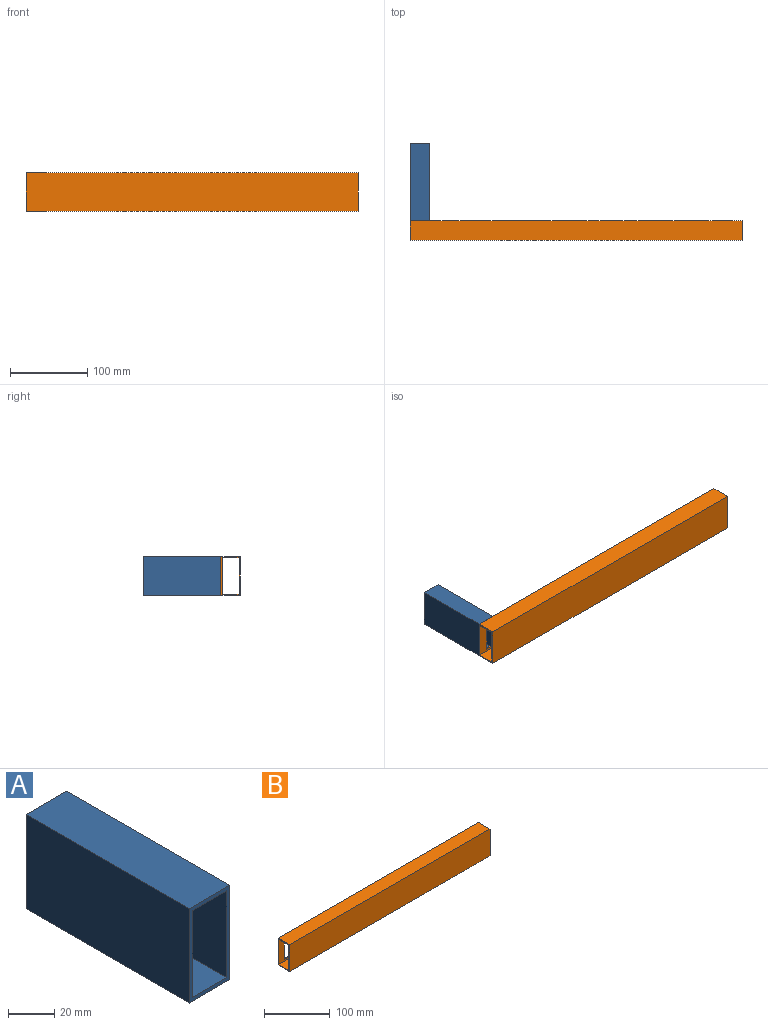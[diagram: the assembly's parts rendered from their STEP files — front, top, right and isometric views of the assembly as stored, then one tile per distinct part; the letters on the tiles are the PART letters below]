
ASSEMBLY  parts=2 mates=1
PART A: 10 faces, bbox 25x100x50 mm
  f0: plane 100x25mm, normal (0,0,1), area 2500mm2, adj f1,f7,f8,f9
  f1: plane 100x50mm, normal (-1,0,0), area 5000mm2, adj f0,f2,f8,f9
  f2: plane 100x25mm, normal (0,0,-1), area 2500mm2, adj f1,f7,f8,f9
  f3: plane 100x21mm, normal (0,0,-1), area 2100mm2, adj f4,f6,f8,f9
  f4: plane 100x46mm, normal (-1,0,0), area 4600mm2, adj f3,f5,f8,f9
  f5: plane 100x21mm, normal (0,0,1), area 2100mm2, adj f4,f6,f8,f9
  f6: plane 100x46mm, normal (1,0,0), area 4600mm2, adj f3,f5,f8,f9
  f7: plane 100x50mm, normal (1,0,0), area 5000mm2, adj f0,f2,f8,f9
  f8: plane 50x25mm, normal (0,-1,0), area 284mm2, adj f0,f1,f2,f3,f4,f5,f6,f7
  f9: plane 50x25mm, normal (0,1,0), area 284mm2, adj f0,f1,f2,f3,f4,f5,f6,f7
PART B: 72 faces, bbox 430x25x50 mm
  f0: plane 430x47mm, normal (0,1,0), area 20210mm2, adj f1,f7,f8,f9
  f1: plane 430x22mm, normal (0,0,-1), area 9460mm2, adj f0,f2,f8,f9
  f2: plane 430x47mm, normal (0,-1,0), area 11386.5mm2, adj f1,f7,f8,f9,f10,f11,f12,f13
  f3: plane 430x50mm, normal (0,1,0), area 12676.5mm2, adj f4,f6,f8,f9,f10,f11,f12,f13
  f4: plane 430x25mm, normal (0,0,1), area 10750mm2, adj f3,f5,f8,f9
  f5: plane 430x50mm, normal (0,-1,0), area 21500mm2, adj f4,f6,f8,f9
  f6: plane 430x25mm, normal (0,0,-1), area 10750mm2, adj f3,f5,f8,f9
  f7: plane 430x22mm, normal (0,0,1), area 9460mm2, adj f0,f2,f8,f9
  f8: plane 50x25mm, normal (1,0,0), area 216mm2, adj f0,f1,f2,f3,f4,f5,f6,f7
  f9: plane 50x25mm, normal (-1,0,0), area 216mm2, adj f0,f1,f2,f3,f4,f5,f6,f7
  f10: plane 40x21.56mm, normal (-0.88,0,-0.47), area 68.2mm2, adj f2,f3,f11,f12
  f11: plane 40x1.5mm, normal (1,0,0), area 60mm2, adj f2,f3,f10,f12
  f12: plane 21.56x1.5mm, normal (0,0,1), area 32.3mm2, adj f2,f3,f10,f11
  f13: plane 40x21.56mm, normal (-0.88,0,-0.47), area 68.2mm2, adj f2,f3,f14,f15
  f14: plane 40x1.5mm, normal (1,0,0), area 60mm2, adj f2,f3,f13,f15
  f15: plane 21.56x1.5mm, normal (0,0,1), area 32.3mm2, adj f2,f3,f13,f14
  f16: plane 40x21.56mm, normal (-0.88,0,-0.47), area 68.2mm2, adj f2,f3,f17,f18
  f17: plane 40x1.5mm, normal (1,0,0), area 60mm2, adj f2,f3,f16,f18
  f18: plane 21.56x1.5mm, normal (0,0,1), area 32.3mm2, adj f2,f3,f16,f17
  f19: plane 40x1.5mm, normal (-1,0,0), area 60mm2, adj f2,f3,f20,f21
  f20: plane 21.56x1.5mm, normal (0,0,-1), area 32.3mm2, adj f2,f3,f19,f21
  f21: plane 40x21.56mm, normal (0.88,0,0.47), area 68.2mm2, adj f2,f3,f19,f20
  f22: plane 40x21.56mm, normal (-0.88,0,-0.47), area 68.2mm2, adj f2,f3,f23,f24
  f23: plane 40x1.5mm, normal (1,0,0), area 60mm2, adj f2,f3,f22,f24
  f24: plane 21.56x1.5mm, normal (0,0,1), area 32.3mm2, adj f2,f3,f22,f23
  f25: plane 40x1.5mm, normal (-1,0,0), area 60mm2, adj f2,f3,f26,f27
  f26: plane 21.56x1.5mm, normal (0,0,-1), area 32.3mm2, adj f2,f3,f25,f27
  f27: plane 40x21.56mm, normal (0.88,0,0.47), area 68.2mm2, adj f2,f3,f25,f26
  f28: plane 21.56x1.5mm, normal (0,0,-1), area 32.3mm2, adj f2,f3,f29,f30
  f29: plane 40x21.56mm, normal (0.88,0,0.47), area 68.2mm2, adj f2,f3,f28,f30
  f30: plane 40x1.5mm, normal (-1,0,0), area 60mm2, adj f2,f3,f28,f29
  f31: plane 40x1.5mm, normal (-1,0,0), area 60mm2, adj f2,f3,f32,f33
  f32: plane 21.56x1.5mm, normal (0,0,-1), area 32.3mm2, adj f2,f3,f31,f33
  f33: plane 40x21.56mm, normal (0.88,0,0.47), area 68.2mm2, adj f2,f3,f31,f32
  f34: plane 40x21.56mm, normal (-0.88,0,-0.47), area 68.2mm2, adj f2,f3,f35,f36
  f35: plane 40x1.5mm, normal (1,0,0), area 60mm2, adj f2,f3,f34,f36
  f36: plane 21.56x1.5mm, normal (0,0,1), area 32.3mm2, adj f2,f3,f34,f35
  f37: plane 40x1.5mm, normal (-1,0,0), area 60mm2, adj f2,f3,f38,f39
  f38: plane 21.56x1.5mm, normal (0,0,-1), area 32.3mm2, adj f2,f3,f37,f39
  f39: plane 40x21.56mm, normal (0.88,0,0.47), area 68.2mm2, adj f2,f3,f37,f38
  f40: plane 40x21.56mm, normal (-0.88,0,-0.47), area 68.2mm2, adj f2,f3,f41,f42
  f41: plane 40x1.5mm, normal (1,0,0), area 60mm2, adj f2,f3,f40,f42
  f42: plane 21.56x1.5mm, normal (0,0,1), area 32.3mm2, adj f2,f3,f40,f41
  f43: plane 40x1.5mm, normal (-1,0,0), area 60mm2, adj f2,f3,f44,f45
  f44: plane 21.56x1.5mm, normal (0,0,-1), area 32.3mm2, adj f2,f3,f43,f45
  f45: plane 40x21.56mm, normal (0.88,0,0.47), area 68.2mm2, adj f2,f3,f43,f44
  f46: plane 40x21.56mm, normal (-0.88,0,-0.47), area 68.2mm2, adj f2,f3,f47,f48
  f47: plane 40x1.5mm, normal (1,0,0), area 60mm2, adj f2,f3,f46,f48
  f48: plane 21.56x1.5mm, normal (0,0,1), area 32.3mm2, adj f2,f3,f46,f47
  f49: plane 40x1.5mm, normal (-1,0,0), area 60mm2, adj f2,f3,f50,f51
  f50: plane 21.56x1.5mm, normal (0,0,-1), area 32.3mm2, adj f2,f3,f49,f51
  f51: plane 40x21.56mm, normal (0.88,0,0.47), area 68.2mm2, adj f2,f3,f49,f50
  f52: plane 40x21.56mm, normal (-0.88,0,-0.47), area 68.2mm2, adj f2,f3,f53,f54
  f53: plane 40x1.5mm, normal (1,0,0), area 60mm2, adj f2,f3,f52,f54
  f54: plane 21.56x1.5mm, normal (0,0,1), area 32.3mm2, adj f2,f3,f52,f53
  f55: plane 40x1.5mm, normal (-1,0,0), area 60mm2, adj f2,f3,f56,f57
  f56: plane 21.56x1.5mm, normal (0,0,-1), area 32.3mm2, adj f2,f3,f55,f57
  f57: plane 40x21.56mm, normal (0.88,0,0.47), area 68.2mm2, adj f2,f3,f55,f56
  f58: plane 40x21.56mm, normal (-0.88,0,-0.47), area 68.2mm2, adj f2,f3,f59,f60
  f59: plane 40x1.5mm, normal (1,0,0), area 60mm2, adj f2,f3,f58,f60
  f60: plane 21.56x1.5mm, normal (0,0,1), area 32.3mm2, adj f2,f3,f58,f59
  f61: plane 40x1.5mm, normal (-1,0,0), area 60mm2, adj f2,f3,f62,f63
  f62: plane 21.56x1.5mm, normal (0,0,-1), area 32.3mm2, adj f2,f3,f61,f63
  f63: plane 40x21.56mm, normal (0.88,0,0.47), area 68.2mm2, adj f2,f3,f61,f62
  f64: cylinder r=6.5mm len=13mm, axis (0,-1,0), area 61.3mm2, adj f2,f3
  f65: cylinder r=6.5mm len=13mm, axis (0,-1,0), area 61.3mm2, adj f2,f3
  f66: cylinder r=6.5mm len=13mm, axis (0,-1,0), area 61.3mm2, adj f2,f3
  f67: cylinder r=6.5mm len=13mm, axis (0,-1,0), area 61.3mm2, adj f2,f3
  f68: cylinder r=6.5mm len=13mm, axis (0,-1,0), area 61.3mm2, adj f2,f3
  f69: cylinder r=6.5mm len=13mm, axis (0,-1,0), area 61.3mm2, adj f2,f3
  f70: cylinder r=6.5mm len=13mm, axis (0,-1,0), area 61.3mm2, adj f2,f3
  f71: cylinder r=6.5mm len=13mm, axis (0,-1,0), area 61.3mm2, adj f2,f3
PLACE A t=(11.47,89.84,-6.53)mm
PLACE B t=(-1.03,-22.66,-8.26)mm
MATE fastened A.f8 <-> B.f3  axis (0,-1,0) through (-1.03,-10.16,-33.26)mm
